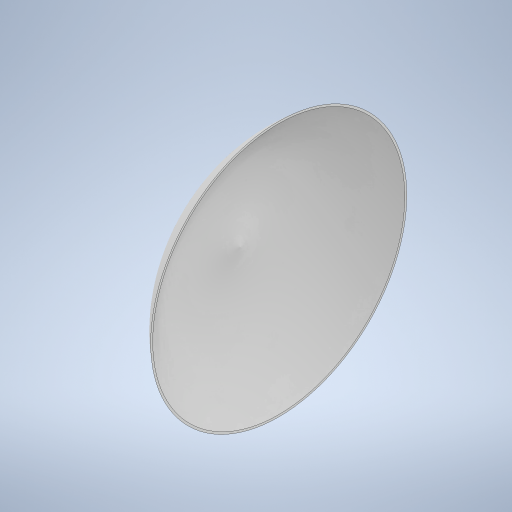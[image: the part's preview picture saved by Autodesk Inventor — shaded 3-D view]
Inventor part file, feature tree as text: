
AUTODESK INVENTOR PART (.ipt)
format: ipt  version: 2023 (Build 270158000, 158)  size: 622,592 bytes
history: native  units: mm
features: revolve x1, shell x1, sketch x1
ambient origin geometry x8: Origin, YZ Plane, XZ Plane, XY Plane, X Axis, Y Axis, Z Axis, Center Point
bodies: Solid1 (feature_tree)
feature tree (3):
  revolve  "Revolution1"  [1 undecoded]
  shell  "Shell1"  Thickness=90.0deg
  sketch  "Sketch1"  dims[d0=25.0mm d1=80.0mm d3=90.0deg d4=1.0mm d6=73.257611mm]
note: 1 required parameter value undecoded (feature->parameter linkage not recoverable at this tier; creation-order binding heuristic only, values carry confidence <= 0.55)
